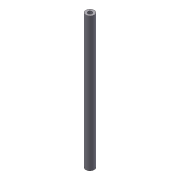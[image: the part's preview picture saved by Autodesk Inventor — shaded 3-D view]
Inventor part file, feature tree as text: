
AUTODESK INVENTOR PART (.ipt)
format: ipt  version: 2012 (Build 160160000, 160)  size: 65,024 bytes
history: native  units: in
note: dims shown in document units (in); Inventor stores cm internally (conversion verified against a paired STEP export)
features: extrude x1, sketch x1
ambient origin geometry x8: Origin, YZ Plane, XZ Plane, XY Plane, X Axis, Y Axis, Z Axis, Center Point
bodies: Solid1 (feature_tree)
feature tree (2):
  extrude  "Extrusion1"  Depth=0.5in
  sketch  "Sketch2"  dims[d0=0.25in d1=0.5in d2=8.0in d3=0.0in]
